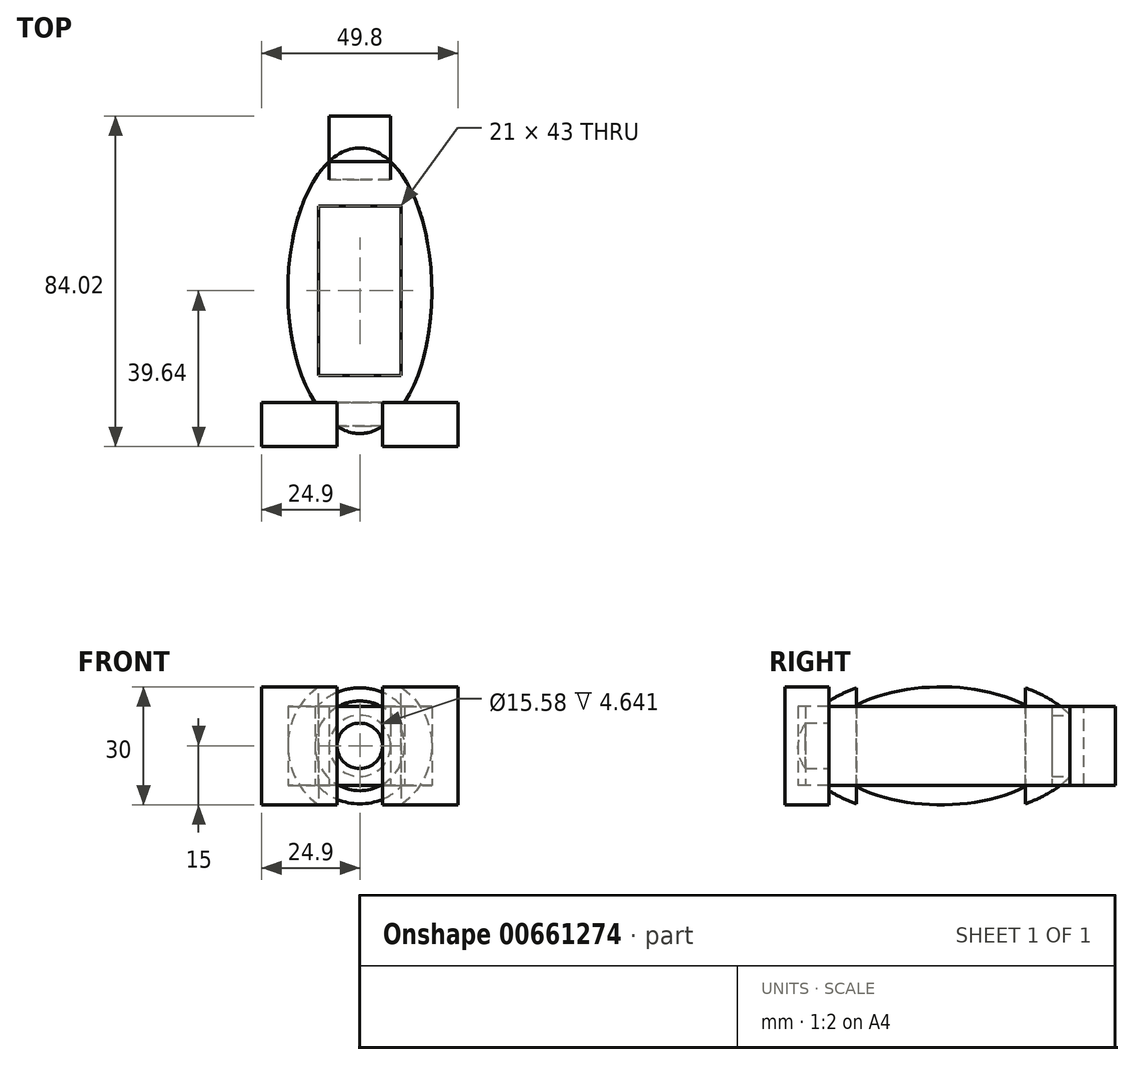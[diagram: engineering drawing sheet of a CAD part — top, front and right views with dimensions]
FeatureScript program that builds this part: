
annotation { "Feature Type Name" : "Feature", "Feature Type Description" : "" }
export const myFeature = defineFeature(function(context is Context, id is Id, definition is map)
    precondition{}
    {
        {
            var Q0;
            Q0=qCreatedBy(makeId("Top.planeOp"),FACE);
            var sketch = newSketch(context, id + "F0", { "sketchPlane" : qUnion([Q0])});
            skEllipse(sketch, "E0", {"center": v(0, 0) * mm, "majorRadius": 36.29 * mm, "minorRadius": 18.29 * mm, "majorAxis": v(0, 1)});
            skLineSegment(sketch, "E1.bottom", {"start": v(-5.78, -28.4) * mm, "end": v(-24.9, -28.4) * mm});
            skLineSegment(sketch, "E1.top", {"start": v(-5.78, -39.64) * mm, "end": v(-24.9, -39.64) * mm});
            skLineSegment(sketch, "E1.left", {"start": v(-5.78, -28.4) * mm, "end": v(-5.78, -39.64) * mm});
            skLineSegment(sketch, "E1.right", {"start": v(-24.9, -28.4) * mm, "end": v(-24.9, -39.64) * mm});
            skLineSegment(sketch, "E2.MirrorCS", {"start": v(5.78, -28.4) * mm, "end": v(24.9, -28.4) * mm});
            skLineSegment(sketch, "E3.MirrorCS", {"start": v(24.9, -28.4) * mm, "end": v(24.9, -39.64) * mm});
            skLineSegment(sketch, "E4.MirrorCS", {"start": v(5.78, -39.64) * mm, "end": v(24.9, -39.64) * mm});
            skLineSegment(sketch, "E5.MirrorCS", {"start": v(5.78, -28.4) * mm, "end": v(5.78, -39.64) * mm});
            skLineSegment(sketch, "E6", {"start": v(0, 36.29) * mm, "end": v(0, -36.29) * mm});
            skLineSegment(sketch, "E7.bottom", {"start": v(-10.5, 21.5) * mm, "end": v(10.5, 21.5) * mm});
            skLineSegment(sketch, "E7.top", {"start": v(-10.5, -21.5) * mm, "end": v(10.5, -21.5) * mm});
            skLineSegment(sketch, "E7.left", {"start": v(-10.5, 21.5) * mm, "end": v(-10.5, -21.5) * mm});
            skLineSegment(sketch, "E7.right", {"start": v(10.5, 21.5) * mm, "end": v(10.5, -21.5) * mm});
            skLineSegment(sketch, "E8.bottom", {"start": v(7.79, 44.38) * mm, "end": v(-7.79, 44.38) * mm});
            skLineSegment(sketch, "E8.top", {"start": v(7.79, 28.2) * mm, "end": v(-7.79, 28.2) * mm});
            skLineSegment(sketch, "E8.left", {"start": v(7.79, 44.38) * mm, "end": v(7.79, 28.2) * mm});
            skLineSegment(sketch, "E8.right", {"start": v(-7.79, 44.38) * mm, "end": v(-7.79, 28.2) * mm});
            skPoint(sketch, "E8.middle", {"position": v(0, 36.29) * mm});
            skSolve(sketch);
        }
        {
            var Q0;
            {var subQ6=sQuery(id+"F0.wireOp",EDGE,"E6");Q0=makeQuery(id+"F0.imprint","IMPRINT",FACE,{"disambiguationData":[TD([[makeQuery(id+"F0.imprint","IMPRINT",EDGE,{"derivedFrom":subQ6}),-1.0]])]});}
            var Q1;
            Q1=sQuery(id+"F0.wireOp",EDGE,"E6");
            revolve(context, id + "F1", {"entities" : qUnion([Q0]), "axis" : qUnion([Q1]), "revolveType" : RevolveType.FULL});
        }
        {
            var Q0;
            {var subQ1=sQuery(id+"F0.wireOp",EDGE,"E1.top");Q0=makeQuery(id+"F0.imprint","IMPRINT",FACE,{"disambiguationData":[TD([[makeQuery(id+"F0.imprint","IMPRINT",EDGE,{"derivedFrom":subQ1}),-1.0]])]});}
            var Q1;
            {var subQ0=sQuery(id+"F0.wireOp",EDGE,"E1.bottom");var subQ1=sQuery(id+"F0.wireOp",EDGE,"E0");var subQ2=makeQuery(id+"F0.imprint","INTERSECT",VERTEX,{"derivedFrom":[subQ1,subQ0]});Q1=makeQuery(id+"F0.imprint","IMPRINT",FACE,{"disambiguationData":[TD([[makeQuery(id+"F0.imprint","IMPRINT",EDGE,{"disambiguationData":[TD([[subQ2,-1.0]])],"derivedFrom":subQ1}),1.0]])]});}
            var Q2;
            {var subQ6=sQuery(id+"F0.wireOp",EDGE,"E3.MirrorCS");Q2=makeQuery(id+"F0.imprint","IMPRINT",FACE,{"disambiguationData":[TD([[makeQuery(id+"F0.imprint","IMPRINT",EDGE,{"derivedFrom":subQ6}),-1.0]])]});}
            var Q3;
            {var subQ0=sQuery(id+"F0.wireOp",EDGE,"E5.MirrorCS");var subQ1=sQuery(id+"F0.wireOp",EDGE,"E0");var subQ2=makeQuery(id+"F0.imprint","INTERSECT",VERTEX,{"derivedFrom":[subQ1,subQ0]});Q3=makeQuery(id+"F0.imprint","IMPRINT",FACE,{"disambiguationData":[TD([[makeQuery(id+"F0.imprint","IMPRINT",EDGE,{"disambiguationData":[TD([[subQ2,-1.0]])],"derivedFrom":subQ1}),1.0]])]});}
            extrude(context, id + "F2", {"entities" : qUnion([Q0, Q1, Q2, Q3]), "endBound" : BoundingType.SYMMETRIC, "depth" : 30 * mm, "offsetDistance" : 25.4 * mm});
        }
        {
            var Q0;
            {var subQ5=sQuery(id+"F0.wireOp",EDGE,"E7.right");Q0=makeQuery(id+"F0.imprint","IMPRINT",FACE,{"disambiguationData":[TD([[makeQuery(id+"F0.imprint","IMPRINT",EDGE,{"derivedFrom":subQ5}),-1.0]])]});}
            var Q1;
            {var subQ5=sQuery(id+"F0.wireOp",EDGE,"E7.left");Q1=makeQuery(id+"F0.imprint","IMPRINT",FACE,{"disambiguationData":[TD([[makeQuery(id+"F0.imprint","IMPRINT",EDGE,{"derivedFrom":subQ5}),1.0]])]});}
            extrude(context, id + "F3", {"entities" : qUnion([Q0, Q1]), "operationType" : NewBodyOperationType.REMOVE, "endBound" : BoundingType.SYMMETRIC, "oppositeDirection" : true, "depth" : 500 * mm, "offsetDistance" : 25 * mm});
        }
        {
            var Q0;
            {var subQ1=sQuery(id+"F0.wireOp",EDGE,"E8.bottom");Q0=makeQuery(id+"F0.imprint","IMPRINT",FACE,{"disambiguationData":[TD([[makeQuery(id+"F0.imprint","IMPRINT",EDGE,{"derivedFrom":subQ1}),1.0]])]});}
            var Q1;
            {var subQ0=sQuery(id+"F0.wireOp",EDGE,"E6");var subQ1=sQuery(id+"F0.wireOp",EDGE,"E0");var subQ2=makeQuery(id+"F0.imprint","INTERSECT",VERTEX,{"disambiguationData":[OD(0.0)],"derivedFrom":[subQ1,subQ0]});Q1=makeQuery(id+"F0.imprint","IMPRINT",FACE,{"disambiguationData":[TD([[makeQuery(id+"F0.imprint","IMPRINT",EDGE,{"disambiguationData":[TD([[subQ2,1.0]])],"derivedFrom":subQ1}),1.0]])]});}
            var Q2;
            {var subQ0=sQuery(id+"F0.wireOp",EDGE,"E6");var subQ1=sQuery(id+"F0.wireOp",EDGE,"E0");var subQ2=makeQuery(id+"F0.imprint","INTERSECT",VERTEX,{"disambiguationData":[OD(0.0)],"derivedFrom":[subQ1,subQ0]});Q2=makeQuery(id+"F0.imprint","IMPRINT",FACE,{"disambiguationData":[TD([[makeQuery(id+"F0.imprint","IMPRINT",EDGE,{"disambiguationData":[TD([[subQ2,-1.0]])],"derivedFrom":subQ1}),1.0]])]});}
            extrude(context, id + "F4", {"entities" : qUnion([Q0, Q1, Q2]), "endBound" : BoundingType.SYMMETRIC, "depth" : 20 * mm, "offsetDistance" : 25 * mm});
        }
    });
